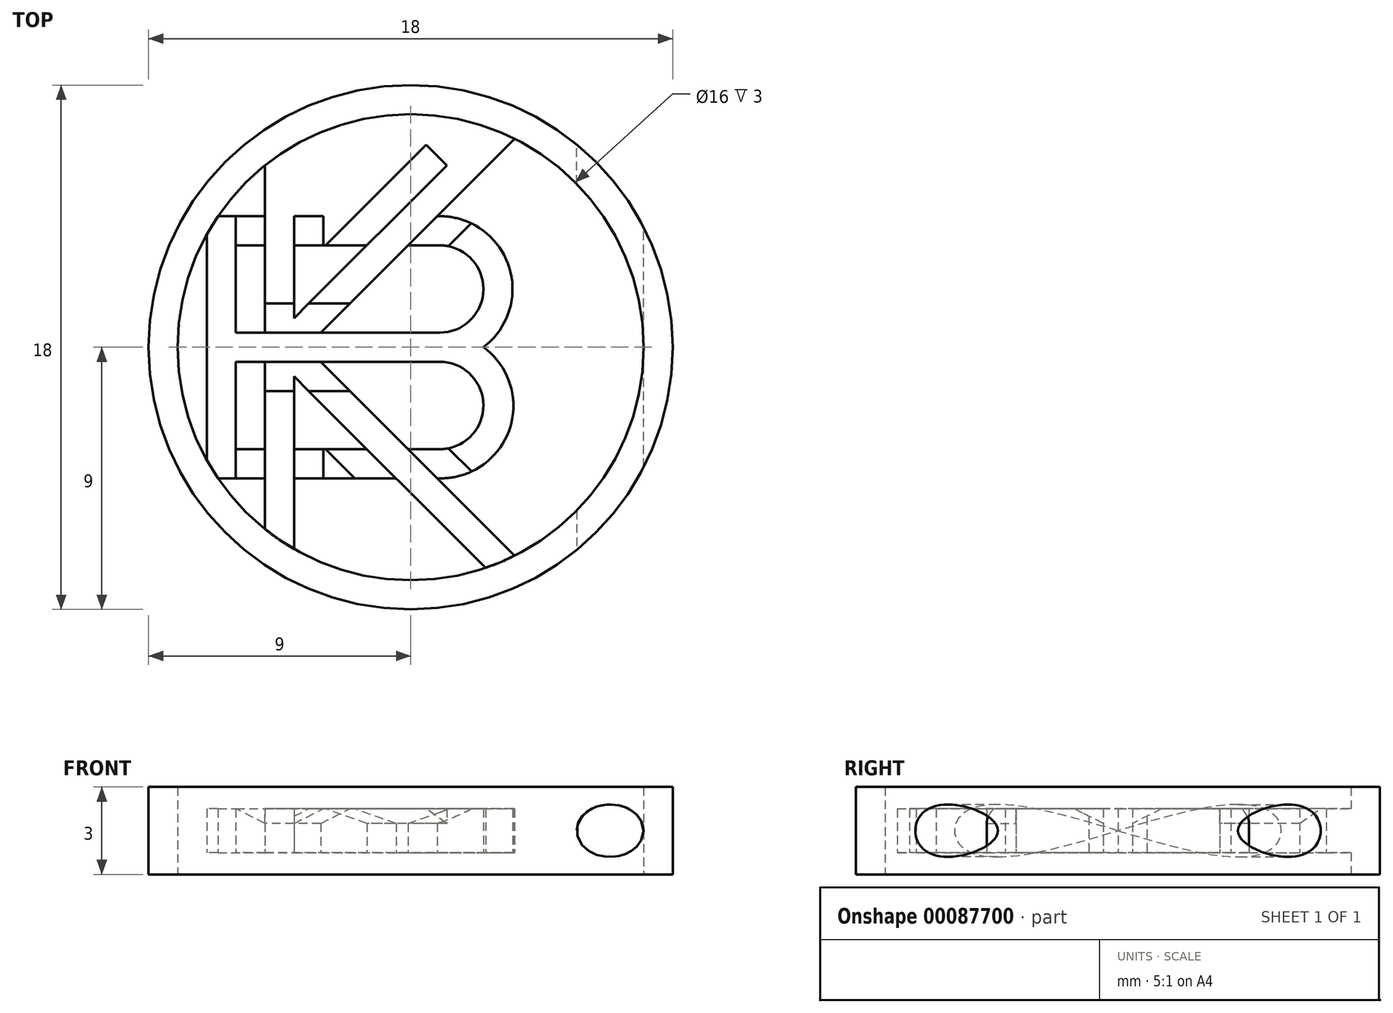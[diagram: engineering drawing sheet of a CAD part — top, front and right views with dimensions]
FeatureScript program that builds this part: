
annotation { "Feature Type Name" : "Feature", "Feature Type Description" : "" }
export const myFeature = defineFeature(function(context is Context, id is Id, definition is map)
    precondition{}
    {
        {
            var Q0;
            Q0=qCreatedBy(makeId("Top.planeOp"),FACE);
            var sketch = newSketch(context, id + "F0", { "sketchPlane" : qUnion([Q0])});
            skCircle(sketch, "E0", {"center": v(0, 0) * mm, "radius": 8 * mm});
            skLineSegment(sketch, "E1", {"start": v(-5, 6.24) * mm, "end": v(-5, -6.24) * mm, "construction": true});
            skLineSegment(sketch, "E2", {"start": v(-4, 6.93) * mm, "end": v(-4, -6.93) * mm, "construction": true});
            skLineSegment(sketch, "E3", {"start": v(-5, 0) * mm, "end": v(2.57, 7.57) * mm, "construction": true});
            skLineSegment(sketch, "E4", {"start": v(-5, 0) * mm, "end": v(2.57, -7.57) * mm, "construction": true});
            skLineSegment(sketch, "E5", {"start": v(-5, -1.41) * mm, "end": v(3.57, 7.16) * mm, "construction": true});
            skLineSegment(sketch, "E6", {"start": v(-5, 1.41) * mm, "end": v(3.57, -7.16) * mm, "construction": true});
            skLineSegment(sketch, "E7", {"start": v(-6.61, 4.5) * mm, "end": v(1, 4.5) * mm, "construction": true});
            skLineSegment(sketch, "E8", {"start": v(-7.2, 3.5) * mm, "end": v(1, 3.5) * mm, "construction": true});
            skLineSegment(sketch, "E9", {"start": v(-7.2, -3.5) * mm, "end": v(1, -3.5) * mm, "construction": true});
            skLineSegment(sketch, "E10", {"start": v(-6.61, -4.5) * mm, "end": v(1, -4.5) * mm, "construction": true});
            skLineSegment(sketch, "E11", {"start": v(-7.98, 0.5) * mm, "end": v(1, 0.5) * mm, "construction": true});
            skLineSegment(sketch, "E12", {"start": v(-7.98, -0.5) * mm, "end": v(1, -0.5) * mm, "construction": true});
            skArc(sketch, "E13", {"start": v(1, -3.5) * mm, "mid": v(2.5, -2) * mm, "end": v(1, -0.5) * mm, "construction": true});
            skArc(sketch, "E14", {"start": v(1, -4.5) * mm, "mid": v(3.5, -2) * mm, "end": v(1, 0.5) * mm, "construction": true});
            skArc(sketch, "E15", {"start": v(1, 0.5) * mm, "mid": v(2.5, 2) * mm, "end": v(1, 3.5) * mm, "construction": true});
            skArc(sketch, "E16", {"start": v(1, 4.5) * mm, "mid": v(3.5, 2) * mm, "end": v(1, -0.5) * mm, "construction": true});
            skLineSegment(sketch, "E17", {"start": v(-5, 3.5) * mm, "end": v(-5, 0.5) * mm});
            skLineSegment(sketch, "E18", {"start": v(-5, -0.5) * mm, "end": v(-5, -3.5) * mm});
            skLineSegment(sketch, "E19", {"start": v(-6.61, -4.5) * mm, "end": v(-5, -4.5) * mm});
            skLineSegment(sketch, "E20", {"start": v(-5, -4.5) * mm, "end": v(-5, -6.24) * mm});
            skLineSegment(sketch, "E21", {"start": v(-6.61, 4.5) * mm, "end": v(-5, 4.5) * mm});
            skLineSegment(sketch, "E22", {"start": v(-5, 4.5) * mm, "end": v(-5, 6.24) * mm});
            skLineSegment(sketch, "E23", {"start": v(-4, 6.93) * mm, "end": v(-4, 4.5) * mm});
            skLineSegment(sketch, "E24", {"start": v(-4, 4.5) * mm, "end": v(1, 4.5) * mm});
            skLineSegment(sketch, "E25", {"start": v(1, 3.5) * mm, "end": v(-0.09, 3.5) * mm});
            skLineSegment(sketch, "E26", {"start": v(-0.09, 3.5) * mm, "end": v(-3.09, 0.5) * mm});
            skLineSegment(sketch, "E27", {"start": v(-3.09, 0.5) * mm, "end": v(1, 0.5) * mm});
            skLineSegment(sketch, "E28", {"start": v(1, -0.5) * mm, "end": v(-3.09, -0.5) * mm});
            skLineSegment(sketch, "E29", {"start": v(-3.09, -0.5) * mm, "end": v(-0.09, -3.5) * mm});
            skLineSegment(sketch, "E30", {"start": v(-0.09, -3.5) * mm, "end": v(1, -3.5) * mm});
            skLineSegment(sketch, "E31", {"start": v(-1.5, 3.5) * mm, "end": v(-4, 3.5) * mm});
            skLineSegment(sketch, "E32", {"start": v(-4, 3.5) * mm, "end": v(-4, 1) * mm});
            skLineSegment(sketch, "E33", {"start": v(-4, 1) * mm, "end": v(-1.5, 3.5) * mm});
            skLineSegment(sketch, "E34", {"start": v(-4, -1) * mm, "end": v(-4, -3.5) * mm});
            skLineSegment(sketch, "E35", {"start": v(-4, -3.5) * mm, "end": v(-1.5, -3.5) * mm});
            skLineSegment(sketch, "E36", {"start": v(-1.5, -3.5) * mm, "end": v(-4, -1) * mm});
            skLineSegment(sketch, "E37", {"start": v(-4, -6.93) * mm, "end": v(-4, -4.5) * mm});
            skLineSegment(sketch, "E38", {"start": v(-4, -4.5) * mm, "end": v(-0.5, -4.5) * mm});
            skLineSegment(sketch, "E39", {"start": v(-0.5, -4.5) * mm, "end": v(2.57, -7.57) * mm});
            skLineSegment(sketch, "E40", {"start": v(2.57, 7.57) * mm, "end": v(-0.5, 4.5) * mm});
            skLineSegment(sketch, "E41", {"start": v(-0.5, 4.5) * mm, "end": v(-4, 4.5) * mm});
            skArc(sketch, "E42", {"start": v(2.5, 0) * mm, "mid": v(3.37, 2.8) * mm, "end": v(1, 4.5) * mm});
            skArc(sketch, "E43", {"start": v(1, -3.5) * mm, "mid": v(2.5, -2) * mm, "end": v(1, -0.5) * mm});
            skArc(sketch, "E44", {"start": v(1, 0.5) * mm, "mid": v(2.5, 2) * mm, "end": v(1, 3.5) * mm});
            skLineSegment(sketch, "E45", {"start": v(-7, 3.87) * mm, "end": v(-7, -3.87) * mm});
            skLineSegment(sketch, "E46", {"start": v(-5, 3.5) * mm, "end": v(-6, 3.5) * mm});
            skLineSegment(sketch, "E47", {"start": v(-6, 3.5) * mm, "end": v(-6, 0.5) * mm});
            skLineSegment(sketch, "E48", {"start": v(-6, 0.5) * mm, "end": v(-5, 0.5) * mm});
            skLineSegment(sketch, "E49", {"start": v(-5, -0.5) * mm, "end": v(-6, -0.5) * mm});
            skLineSegment(sketch, "E50", {"start": v(-6, -0.5) * mm, "end": v(-6, -3.5) * mm});
            skLineSegment(sketch, "E51", {"start": v(-6, -3.5) * mm, "end": v(-5, -3.5) * mm});
            skLineSegment(sketch, "E52", {"start": v(0.91, 4.5) * mm, "end": v(3.57, 7.16) * mm});
            skLineSegment(sketch, "E53", {"start": v(0.91, -4.5) * mm, "end": v(3.57, -7.16) * mm});
            skLineSegment(sketch, "E54", {"start": v(0.91, -4.5) * mm, "end": v(1, -4.5) * mm});
            skArc(sketch, "E55", {"start": v(1, -4.5) * mm, "mid": v(3.4, -2.8) * mm, "end": v(2.5, 0) * mm});
            skSolve(sketch);
        }
        {
            var Q0;
            Q0=qCreatedBy(makeId("Top.planeOp"),FACE);
            var sketch = newSketch(context, id + "F1", { "sketchPlane" : qUnion([Q0])});
            skCircle(sketch, "E56", {"center": v(0, 0) * mm, "radius": 9 * mm});
            skCircle(sketch, "E57", {"center": v(0, 0) * mm, "radius": 8 * mm});
            skSolve(sketch);
        }
        {
            var Q0;
            Q0 = qSketchRegion(id + "F1", true);
            extrude(context, id + "F2", {"entities" : qUnion([Q0]), "depth" : 2.25 * mm, "hasSecondDirection" : true, "secondDirectionOppositeDirection" : true, "secondDirectionDepth" : .75 * mm});
        }
        {
            var Q0;
            Q0=makeQuery(id+"F0.imprint","IMPRINT",FACE,{"disambiguationData":[TD([[makeQuery(id+"F0.imprint","IMPRINT",EDGE,{"derivedFrom":sQuery(id+"F0.wireOp",EDGE,"E17")}),1.0]])]});
            var Q1;
            {var subQ1=sQuery(id+"F0.wireOp",EDGE,"E24");Q1=makeQuery(id+"F0.imprint","IMPRINT",FACE,{"disambiguationData":[TD([[makeQuery(id+"F0.imprint","IMPRINT",EDGE,{"derivedFrom":subQ1}),1.0]])]});}
            extrude(context, id + "F3", {"entities" : qUnion([Q0, Q1]), "operationType" : NewBodyOperationType.ADD, "depth" : 1.5 * mm});
        }
        {
            var Q0;
            Q0=makeQuery(id+"F3.opExtrude","CAP_EDGE",EDGE,{"disambiguationData":[OSD([sQuery(id+"F0.wireOp",EDGE,"E29")])],"isStart":false});
            cPlane(context, id + "F4", {"entities" : qUnion([Q0]), "cplaneType" : CPlaneType.MID_PLANE, "offset" : 150 * mm, "width" : 150 * mm, "height" : 150 * mm});
        }
        {
            var Q0;
            Q0=makeQuery(id+"F3.opExtrude","CAP_EDGE",EDGE,{"disambiguationData":[OSD([sQuery(id+"F0.wireOp",EDGE,"E26")])],"isStart":false});
            cPlane(context, id + "F5", {"entities" : qUnion([Q0]), "cplaneType" : CPlaneType.MID_PLANE, "offset" : 150 * mm, "width" : 150 * mm, "height" : 150 * mm});
        }
        {
            var Q0;
            Q0=qCreatedBy(makeId("Front.planeOp"),FACE);
            var sketch = newSketch(context, id + "F6", { "sketchPlane" : qUnion([Q0])});
            skEllipse(sketch, "E58", {"center": v(6.85, 0.75) * mm, "majorRadius": 1.15 * mm, "minorRadius": 0.9 * mm, "majorAxis": v(1, 0)});
            skSolve(sketch);
        }
        {
            var Q0;
            Q0=makeQuery(id+"F6.imprint","IMPRINT",FACE,{"disambiguationData":[TD([[makeQuery(id+"F6.imprint","IMPRINT",EDGE,{"derivedFrom":sQuery(id+"F6.wireOp",EDGE,"E58")}),1.0]])]});
            extrude(context, id + "F7", {"entities" : qUnion([Q0]), "operationType" : NewBodyOperationType.REMOVE, "depth" : 25 * mm, "hasSecondDirection" : true, "secondDirectionOppositeDirection" : true, "secondDirectionDepth" : 25 * mm});
        }
        {
            var Q0;
            Q0=makeQuery(id+"F3.opExtrude","SWEPT_FACE",FACE,{"disambiguationData":[OSD([sQuery(id+"F0.wireOp",EDGE,"E31")])]});
            var sketch = newSketch(context, id + "F8", { "sketchPlane" : qUnion([Q0])});
            skLineSegment(sketch, "E59", {"start": v(-4, 1) * mm, "end": v(-3, 1.5) * mm});
            skSolve(sketch);
        }
        {
            var Q0;
            {var subQ0=sQuery(id+"F8.wireOp",EDGE,"E59");Q0=makeQuery(id+"F8.imprint","IMPRINT",FACE,{"disambiguationData":[TD([[makeQuery(id+"F8.imprint","IMPRINT",EDGE,{"derivedFrom":subQ0}),1.0]])]});}
            extrude(context, id + "F9", {"entities" : qUnion([Q0]), "operationType" : NewBodyOperationType.REMOVE, "oppositeDirection" : true, "depth" : 1 * mm});
        }
        {
            var Q0;
            Q0=makeQuery(id+"F3.opExtrude","SWEPT_FACE",FACE,{"disambiguationData":[OSD([sQuery(id+"F0.wireOp",EDGE,"E46")])]});
            var sketch = newSketch(context, id + "F10", { "sketchPlane" : qUnion([Q0])});
            skLineSegment(sketch, "E60", {"start": v(-5, 1) * mm, "end": v(-6, 1.5) * mm});
            skSolve(sketch);
        }
        {
            var Q0;
            {var subQ0=sQuery(id+"F10.wireOp",EDGE,"E60");Q0=makeQuery(id+"F10.imprint","IMPRINT",FACE,{"disambiguationData":[TD([[makeQuery(id+"F10.imprint","IMPRINT",EDGE,{"derivedFrom":subQ0}),-1.0]])]});}
            extrude(context, id + "F11", {"entities" : qUnion([Q0]), "operationType" : NewBodyOperationType.REMOVE, "oppositeDirection" : true, "depth" : 1 * mm});
        }
        {
            var Q0;
            Q0=makeQuery(id+"F3.opExtrude","SWEPT_FACE",FACE,{"disambiguationData":[OSD([sQuery(id+"F0.wireOp",EDGE,"E51")])]});
            var sketch = newSketch(context, id + "F12", { "sketchPlane" : qUnion([Q0])});
            skLineSegment(sketch, "E61", {"start": v(5, 1) * mm, "end": v(6, 1.5) * mm});
            skSolve(sketch);
        }
        {
            var Q0;
            {var subQ0=sQuery(id+"F12.wireOp",EDGE,"E61");Q0=makeQuery(id+"F12.imprint","IMPRINT",FACE,{"disambiguationData":[TD([[makeQuery(id+"F12.imprint","IMPRINT",EDGE,{"derivedFrom":subQ0}),1.0]])]});}
            extrude(context, id + "F13", {"entities" : qUnion([Q0]), "operationType" : NewBodyOperationType.REMOVE, "oppositeDirection" : true, "depth" : 1 * mm});
        }
        {
            var Q0;
            Q0=makeQuery(id+"F3.opExtrude","SWEPT_FACE",FACE,{"disambiguationData":[OSD([sQuery(id+"F0.wireOp",EDGE,"E35")])]});
            var sketch = newSketch(context, id + "F14", { "sketchPlane" : qUnion([Q0])});
            skLineSegment(sketch, "E62", {"start": v(4, 1) * mm, "end": v(3, 1.5) * mm});
            skSolve(sketch);
        }
        {
            var Q0;
            {var subQ0=sQuery(id+"F14.wireOp",EDGE,"E62");Q0=makeQuery(id+"F14.imprint","IMPRINT",FACE,{"disambiguationData":[TD([[makeQuery(id+"F14.imprint","IMPRINT",EDGE,{"derivedFrom":subQ0}),-1.0]])]});}
            extrude(context, id + "F15", {"entities" : qUnion([Q0]), "operationType" : NewBodyOperationType.REMOVE, "oppositeDirection" : true, "depth" : 1 * mm});
        }
        {
            var Q0;
            {var subQ0=sQuery(id+"F0.wireOp",EDGE,"E17");Q0=makeQuery(id+"F11.boolean.opBoolean","MERGE",FACE,{"derivedFrom":[makeQuery(id+"F3.opExtrude","SWEPT_FACE",FACE,{"disambiguationData":[OSD([subQ0])]}),makeQuery(id+"F3.opExtrude","SWEPT_FACE",FACE,{"disambiguationData":[OSD([sQuery(id+"F0.wireOp",EDGE,"E22")])]}),makeQuery(id+"F11.opExtrude","SWEPT_FACE",FACE,{"disambiguationData":[OSD([subQ0,sQuery(id+"F0.wireOp",EDGE,"E46")])]})]});}
            var sketch = newSketch(context, id + "F16", { "sketchPlane" : qUnion([Q0])});
            skLineSegment(sketch, "E63", {"start": v(-1.5, 1.5) * mm, "end": v(-0.5, 1) * mm});
            skSolve(sketch);
        }
        {
            var Q0;
            {var subQ0=sQuery(id+"F16.wireOp",EDGE,"E63");Q0=makeQuery(id+"F16.imprint","IMPRINT",FACE,{"disambiguationData":[TD([[makeQuery(id+"F16.imprint","IMPRINT",EDGE,{"derivedFrom":subQ0}),1.0]])]});}
            extrude(context, id + "F17", {"entities" : qUnion([Q0]), "operationType" : NewBodyOperationType.REMOVE, "oppositeDirection" : true, "depth" : 3 * mm});
        }
        {
            var Q0;
            {var subQ0=sQuery(id+"F0.wireOp",EDGE,"E18");Q0=makeQuery(id+"F13.boolean.opBoolean","MERGE",FACE,{"derivedFrom":[makeQuery(id+"F3.opExtrude","SWEPT_FACE",FACE,{"disambiguationData":[OSD([subQ0])]}),makeQuery(id+"F3.opExtrude","SWEPT_FACE",FACE,{"disambiguationData":[OSD([sQuery(id+"F0.wireOp",EDGE,"E20")])]}),makeQuery(id+"F13.opExtrude","SWEPT_FACE",FACE,{"disambiguationData":[OSD([subQ0,sQuery(id+"F0.wireOp",EDGE,"E51")])]})]});}
            var sketch = newSketch(context, id + "F18", { "sketchPlane" : qUnion([Q0])});
            skLineSegment(sketch, "E64", {"start": v(0.5, 1) * mm, "end": v(1.5, 1.5) * mm});
            skSolve(sketch);
        }
        {
            var Q0;
            {var subQ0=sQuery(id+"F18.wireOp",EDGE,"E64");Q0=makeQuery(id+"F18.imprint","IMPRINT",FACE,{"disambiguationData":[TD([[makeQuery(id+"F18.imprint","IMPRINT",EDGE,{"derivedFrom":subQ0}),1.0]])]});}
            extrude(context, id + "F19", {"entities" : qUnion([Q0]), "operationType" : NewBodyOperationType.REMOVE, "oppositeDirection" : true, "depth" : 3 * mm});
        }
        {
            var Q0;
            Q0=qCreatedBy(id+"F5.planeOp",FACE);
            var sketch = newSketch(context, id + "F20", { "sketchPlane" : qUnion([Q0])});
            skLineSegment(sketch, "E65", {"start": v(-4.54, 1.5) * mm, "end": v(-3.54, 1.5) * mm});
            skLineSegment(sketch, "E66", {"start": v(-3.54, 1.5) * mm, "end": v(-3.54, 1) * mm});
            skLineSegment(sketch, "E67", {"start": v(-3.54, 1) * mm, "end": v(-4.54, 1.5) * mm});
            skLineSegment(sketch, "E68", {"start": v(-1.54, 1.5) * mm, "end": v(-2.54, 1.5) * mm});
            skLineSegment(sketch, "E69", {"start": v(-2.54, 1.5) * mm, "end": v(-2.54, 1) * mm});
            skLineSegment(sketch, "E70", {"start": v(-2.54, 1) * mm, "end": v(-1.54, 1.5) * mm});
            skSolve(sketch);
        }
        {
            var Q0;
            Q0=makeQuery(id+"F20.imprint","IMPRINT",FACE,{"disambiguationData":[TD([[makeQuery(id+"F20.imprint","IMPRINT",EDGE,{"derivedFrom":sQuery(id+"F20.wireOp",EDGE,"E65")}),-1.0]])]});
            var Q1;
            Q1=makeQuery(id+"F20.imprint","IMPRINT",FACE,{"disambiguationData":[TD([[makeQuery(id+"F20.imprint","IMPRINT",EDGE,{"derivedFrom":sQuery(id+"F20.wireOp",EDGE,"E68")}),1.0]])]});
            extrude(context, id + "F21", {"entities" : qUnion([Q0, Q1]), "operationType" : NewBodyOperationType.REMOVE, "oppositeDirection" : true, "depth" : 5 * mm});
        }
        {
            var Q0;
            Q0=qCreatedBy(id+"F4.planeOp",FACE);
            var sketch = newSketch(context, id + "F22", { "sketchPlane" : qUnion([Q0])});
            skLineSegment(sketch, "E71", {"start": v(-1.54, 1.5) * mm, "end": v(-2.54, 1.5) * mm});
            skLineSegment(sketch, "E72", {"start": v(-2.54, 1.5) * mm, "end": v(-2.54, 1) * mm});
            skLineSegment(sketch, "E73", {"start": v(-2.54, 1) * mm, "end": v(-1.54, 1.5) * mm});
            skLineSegment(sketch, "E74", {"start": v(-4.54, 1.5) * mm, "end": v(-3.54, 1.5) * mm});
            skLineSegment(sketch, "E75", {"start": v(-3.54, 1.5) * mm, "end": v(-3.54, 1) * mm});
            skLineSegment(sketch, "E76", {"start": v(-3.54, 1) * mm, "end": v(-4.54, 1.5) * mm});
            skSolve(sketch);
        }
        {
            var Q0;
            Q0=makeQuery(id+"F22.imprint","IMPRINT",FACE,{"disambiguationData":[TD([[makeQuery(id+"F22.imprint","IMPRINT",EDGE,{"derivedFrom":sQuery(id+"F22.wireOp",EDGE,"E71")}),1.0]])]});
            var Q1;
            Q1=makeQuery(id+"F22.imprint","IMPRINT",FACE,{"disambiguationData":[TD([[makeQuery(id+"F22.imprint","IMPRINT",EDGE,{"derivedFrom":sQuery(id+"F22.wireOp",EDGE,"E74")}),-1.0]])]});
            extrude(context, id + "F23", {"entities" : qUnion([Q0, Q1]), "operationType" : NewBodyOperationType.REMOVE, "depth" : 5 * mm});
        }
    });
